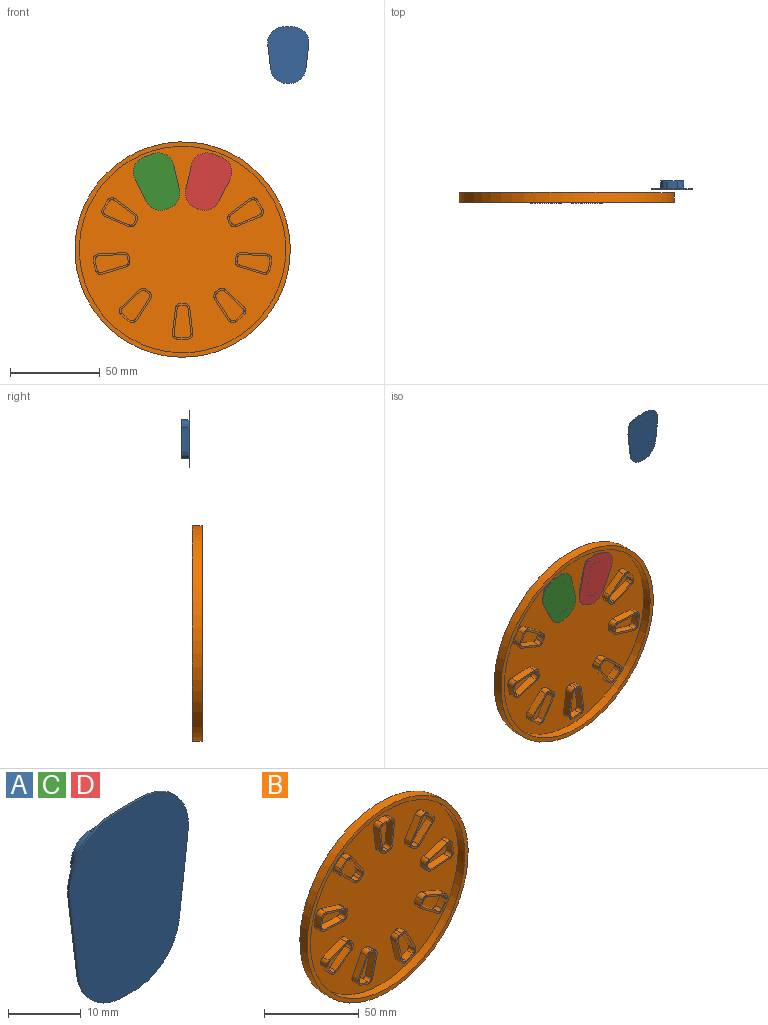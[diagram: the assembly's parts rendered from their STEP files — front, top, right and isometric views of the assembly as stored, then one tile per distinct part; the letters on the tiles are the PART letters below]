
ASSEMBLY  parts=4 mates=2
PART A: 28 faces, bbox 23.1x4.8x31.6 mm
  f0: plane 13.94x4.4mm, normal (-0.99,0,-0.12), area 61.8mm2, adj f1,f15,f16,f26
  f1: cylinder r=3.8mm len=4.4mm, axis (0,-1,0), area 24.7mm2, adj f0,f2,f16,f26
  f2: cylinder r=29.2mm len=4.4mm, axis (0,-1,0), area 8mm2, adj f1,f3,f16,f26
  f3: cylinder r=3.8mm len=4.4mm, axis (0,-1,0), area 24.7mm2, adj f2,f4,f16,f26
  f4: plane 13.94x4.4mm, normal (0.99,0,-0.12), area 61.8mm2, adj f3,f5,f16,f26
  f5: cylinder r=3.8mm len=4.4mm, axis (0,-1,0), area 27.3mm2, adj f4,f6,f16,f26
  f6: cylinder r=50.8mm len=5.92mm, axis (0,-1,0), area 26.1mm2, adj f5,f15,f16,f26
  f7: cylinder r=3.2mm len=4.4mm, axis (0,-1,0), area 23mm2, adj f8,f14,f16,f27
  f8: cylinder r=50.2mm len=5.85mm, axis (0,-1,0), area 25.8mm2, adj f7,f9,f16,f27
  f9: cylinder r=3.2mm len=4.4mm, axis (0,-1,0), area 23mm2, adj f8,f10,f16,f27
  f10: plane 13.94x4.4mm, normal (-0.99,0,0.12), area 61.8mm2, adj f9,f11,f16,f27
  f11: cylinder r=3.2mm len=4.4mm, axis (0,-1,0), area 20.8mm2, adj f10,f12,f16,f27
  f12: cylinder r=29.8mm len=4.4mm, axis (0,-1,0), area 8.2mm2, adj f11,f13,f16,f27
  f13: cylinder r=3.2mm len=4.4mm, axis (0,-1,0), area 20.8mm2, adj f12,f14,f16,f27
  f14: plane 13.94x4.4mm, normal (0.99,0,0.12), area 61.8mm2, adj f7,f13,f16,f27
  f15: cylinder r=3.8mm len=4.4mm, axis (0,-1,0), area 27.3mm2, adj f0,f6,f16,f26
  f16: plane 21.62x13.08mm, normal (0,1,0), area 34.6mm2, adj f0,f1,f2,f3,f4,f5,f6,f7
  f17: plane 31.62x23.08mm, normal (0,-1,0), area 609.5mm2, adj f18,f19,f20,f21,f22,f23,f24,f25
  f18: cylinder r=8.8mm len=9.86mm, axis (0,1,0), area 5.8mm2, adj f17,f19,f25,f26
  f19: plane 13.94x1.71mm, normal (0.99,0,-0.12), area 5.6mm2, adj f17,f18,f20,f26
  f20: cylinder r=8.8mm len=9.01mm, axis (0,1,0), area 5.2mm2, adj f17,f19,f21,f26
  f21: cylinder r=24.2mm len=1.51mm, axis (0,1,0), area 0.6mm2, adj f17,f20,f22,f26
  f22: cylinder r=8.8mm len=9.01mm, axis (0,1,0), area 5.2mm2, adj f17,f21,f23,f26
  f23: plane 13.94x1.71mm, normal (-0.99,0,-0.12), area 5.6mm2, adj f17,f22,f24,f26
  f24: cylinder r=8.8mm len=9.86mm, axis (0,1,0), area 5.8mm2, adj f17,f23,f25,f26
  f25: cylinder r=55.8mm len=6.5mm, axis (0,1,0), area 2.6mm2, adj f17,f18,f24,f26
  f26: plane 31.62x23.08mm, normal (0,1,0), area 376mm2, adj f0,f1,f2,f3,f4,f5,f6,f15
  f27: plane 20.42x11.88mm, normal (0,1,0), area 198.9mm2, adj f7,f8,f9,f10,f11,f12,f13,f14
PART B: 167 faces, bbox 120x5.4x120 mm
  f0: plane 115x115mm, normal (0,-1,0), area 8696mm2, adj f3,f5,f6,f7,f8,f9,f10,f11
  f1: cylinder r=60mm len=120mm, axis (0,1,0), area 2035.8mm2, adj f2,f4
  f2: plane 120x120mm, normal (0,1,0), area 11309.7mm2, adj f1
  f3: cylinder r=57.5mm len=115mm, axis (0,1,0), area 1806.4mm2, adj f0,f4
  f4: plane 120x120mm, normal (0,-1,0), area 922.8mm2, adj f1,f3
  f5: plane 13.94x4.5mm, normal (0.99,0,-0.12), area 63.2mm2, adj f0,f6,f20,f21
  f6: cylinder r=3mm len=4.5mm, axis (0,1,0), area 22.1mm2, adj f0,f5,f7,f21
  f7: cylinder r=50mm len=5.83mm, axis (0,1,0), area 26.2mm2, adj f0,f6,f8,f21
  f8: cylinder r=3mm len=4.5mm, axis (0,1,0), area 22.1mm2, adj f0,f7,f9,f21
  f9: plane 13.94x4.5mm, normal (-0.99,0,-0.12), area 63.2mm2, adj f0,f8,f10,f21
  f10: cylinder r=3mm len=4.5mm, axis (0,1,0), area 20mm2, adj f0,f9,f11,f21
  f11: cylinder r=30mm len=4.5mm, axis (0,1,0), area 8.4mm2, adj f0,f10,f20,f21
  f12: cylinder r=2mm len=4.5mm, axis (0,1,0), area 14.7mm2, adj f13,f19,f21,f22
  f13: cylinder r=49mm len=5.71mm, axis (0,1,0), area 25.7mm2, adj f12,f14,f21,f22
  f14: cylinder r=2mm len=4.5mm, axis (0,1,0), area 14.7mm2, adj f13,f15,f21,f22
  f15: plane 13.94x4.5mm, normal (-0.99,0,0.12), area 63.2mm2, adj f14,f16,f21,f22
  f16: cylinder r=2mm len=4.5mm, axis (0,1,0), area 13.3mm2, adj f15,f17,f21,f22
  f17: cylinder r=31mm len=4.5mm, axis (0,1,0), area 8.7mm2, adj f16,f18,f21,f22
  f18: cylinder r=2mm len=4.5mm, axis (0,1,0), area 13.3mm2, adj f17,f19,f21,f22
  f19: plane 13.94x4.5mm, normal (0.99,0,0.12), area 63.2mm2, adj f12,f18,f21,f22
  f20: cylinder r=3mm len=4.5mm, axis (0,1,0), area 20mm2, adj f0,f5,f11,f21
  f21: plane 20.02x11.48mm, normal (0,-1,0), area 51.3mm2, adj f5,f6,f7,f8,f9,f10,f11,f12
  f22: plane 18.02x9.48mm, normal (0,-1,0), area 136.6mm2, adj f12,f13,f14,f15,f16,f17,f18,f19
  f23: cylinder r=3mm len=4.5mm, axis (0,1,0), area 22.1mm2, adj f0,f24,f38,f39
  f24: cylinder r=50mm len=4.5mm, axis (0,1,0), area 26.2mm2, adj f0,f23,f25,f39
  f25: cylinder r=3mm len=4.5mm, axis (0,1,0), area 22.1mm2, adj f0,f24,f26,f39
  f26: plane 10.27x9.58mm, normal (-0.68,0,-0.73), area 63.2mm2, adj f0,f25,f27,f39
  f27: cylinder r=3mm len=4.5mm, axis (0,1,0), area 20mm2, adj f0,f26,f28,f39
  f28: cylinder r=30mm len=4.5mm, axis (0,1,0), area 8.4mm2, adj f0,f27,f29,f39
  f29: cylinder r=3mm len=4.5mm, axis (0,1,0), area 20mm2, adj f0,f28,f38,f39
  f30: cylinder r=2mm len=4.5mm, axis (0,1,0), area 13.3mm2, adj f31,f37,f39,f40
  f31: cylinder r=31mm len=4.5mm, axis (0,1,0), area 8.7mm2, adj f30,f32,f39,f40
  f32: cylinder r=2mm len=4.5mm, axis (0,1,0), area 13.3mm2, adj f31,f33,f39,f40
  f33: plane 10.27x9.58mm, normal (0.68,0,0.73), area 63.2mm2, adj f32,f34,f39,f40
  f34: cylinder r=2mm len=4.5mm, axis (0,1,0), area 14.7mm2, adj f33,f35,f39,f40
  f35: cylinder r=49mm len=4.5mm, axis (0,1,0), area 25.7mm2, adj f34,f36,f39,f40
  f36: cylinder r=2mm len=4.5mm, axis (0,1,0), area 14.7mm2, adj f35,f37,f39,f40
  f37: plane 11.78x7.65mm, normal (-0.84,0,-0.54), area 63.2mm2, adj f30,f36,f39,f40
  f38: plane 11.78x7.65mm, normal (0.84,0,0.54), area 63.2mm2, adj f0,f23,f29,f39
  f39: plane 19.1x17.84mm, normal (0,-1,0), area 51.3mm2, adj f23,f24,f25,f26,f27,f28,f29,f30
  f40: plane 17.1x15.84mm, normal (0,-1,0), area 136.6mm2, adj f30,f31,f32,f33,f34,f35,f36,f37
  f41: cylinder r=3mm len=4.5mm, axis (0,1,0), area 22.1mm2, adj f0,f42,f56,f57
  f42: cylinder r=50mm len=5.74mm, axis (0,1,0), area 26.2mm2, adj f0,f41,f43,f57
  f43: cylinder r=3mm len=4.5mm, axis (0,1,0), area 22.1mm2, adj f0,f42,f44,f57
  f44: plane 14.02x4.5mm, normal (-0.05,0,-1), area 63.2mm2, adj f0,f43,f45,f57
  f45: cylinder r=3mm len=4.5mm, axis (0,1,0), area 20mm2, adj f0,f44,f46,f57
  f46: cylinder r=30mm len=4.5mm, axis (0,1,0), area 8.4mm2, adj f0,f45,f47,f57
  f47: cylinder r=3mm len=4.5mm, axis (0,1,0), area 20mm2, adj f0,f46,f56,f57
  f48: cylinder r=2mm len=4.5mm, axis (0,1,0), area 13.3mm2, adj f49,f55,f57,f58
  f49: cylinder r=31mm len=4.5mm, axis (0,1,0), area 8.7mm2, adj f48,f50,f57,f58
  f50: cylinder r=2mm len=4.5mm, axis (0,1,0), area 13.3mm2, adj f49,f51,f57,f58
  f51: plane 14.02x4.5mm, normal (0.05,0,1), area 63.2mm2, adj f50,f52,f57,f58
  f52: cylinder r=2mm len=4.5mm, axis (0,1,0), area 14.7mm2, adj f51,f53,f57,f58
  f53: cylinder r=49mm len=5.62mm, axis (0,1,0), area 25.7mm2, adj f52,f54,f57,f58
  f54: cylinder r=2mm len=4.5mm, axis (0,1,0), area 14.7mm2, adj f53,f55,f57,f58
  f55: plane 13.43x4.5mm, normal (-0.29,0,-0.96), area 63.2mm2, adj f48,f54,f57,f58
  f56: plane 13.43x4.5mm, normal (0.29,0,0.96), area 63.2mm2, adj f0,f41,f47,f57
  f57: plane 20.38x12.13mm, normal (0,-1,0), area 51.3mm2, adj f41,f42,f43,f44,f45,f46,f47,f48
  f58: plane 18.38x10.13mm, normal (0,-1,0), area 136.6mm2, adj f48,f49,f50,f51,f52,f53,f54,f55
  f59: cylinder r=3mm len=4.5mm, axis (0,1,0), area 22.1mm2, adj f0,f60,f74,f75
  f60: cylinder r=50mm len=5.05mm, axis (0,1,0), area 26.2mm2, adj f0,f59,f61,f75
  f61: cylinder r=3mm len=4.5mm, axis (0,1,0), area 22.1mm2, adj f0,f60,f62,f75
  f62: plane 11.21x8.45mm, normal (0.6,0,-0.8), area 63.2mm2, adj f0,f61,f63,f75
  f63: cylinder r=3mm len=4.5mm, axis (0,1,0), area 20mm2, adj f0,f62,f64,f75
  f64: cylinder r=30mm len=4.5mm, axis (0,1,0), area 8.4mm2, adj f0,f63,f65,f75
  f65: cylinder r=3mm len=4.5mm, axis (0,1,0), area 20mm2, adj f0,f64,f74,f75
  f66: cylinder r=2mm len=4.5mm, axis (0,1,0), area 13.3mm2, adj f67,f73,f75,f76
  f67: cylinder r=31mm len=4.5mm, axis (0,1,0), area 8.7mm2, adj f66,f68,f75,f76
  f68: cylinder r=2mm len=4.5mm, axis (0,1,0), area 13.3mm2, adj f67,f69,f75,f76
  f69: plane 11.21x8.45mm, normal (-0.6,0,0.8), area 63.2mm2, adj f68,f70,f75,f76
  f70: cylinder r=2mm len=4.5mm, axis (0,1,0), area 14.7mm2, adj f69,f71,f75,f76
  f71: cylinder r=49mm len=4.95mm, axis (0,1,0), area 25.7mm2, adj f70,f72,f75,f76
  f72: cylinder r=2mm len=4.5mm, axis (0,1,0), area 14.7mm2, adj f71,f73,f75,f76
  f73: plane 12.92x5.49mm, normal (0.39,0,-0.92), area 63.2mm2, adj f66,f72,f75,f76
  f74: plane 12.92x5.49mm, normal (-0.39,0,0.92), area 63.2mm2, adj f0,f59,f65,f75
  f75: plane 19.95x16.23mm, normal (0,-1,0), area 51.3mm2, adj f59,f60,f61,f62,f63,f64,f65,f66
  f76: plane 17.95x14.23mm, normal (0,-1,0), area 136.6mm2, adj f66,f67,f68,f69,f70,f71,f72,f73
  f77: cylinder r=3mm len=4.5mm, axis (0,1,0), area 22.1mm2, adj f0,f78,f92,f93
  f78: cylinder r=50mm len=5.48mm, axis (0,1,0), area 26.2mm2, adj f0,f77,f79,f93
  f79: cylinder r=3mm len=4.5mm, axis (0,1,0), area 22.1mm2, adj f0,f78,f80,f93
  f80: plane 13.68x4.5mm, normal (0.97,0,-0.22), area 63.2mm2, adj f0,f79,f81,f93
  f81: cylinder r=3mm len=4.5mm, axis (0,1,0), area 20mm2, adj f0,f80,f82,f93
  f82: cylinder r=30mm len=4.5mm, axis (0,1,0), area 8.4mm2, adj f0,f81,f83,f93
  f83: cylinder r=3mm len=4.5mm, axis (0,1,0), area 20mm2, adj f0,f82,f92,f93
  f84: cylinder r=2mm len=4.5mm, axis (0,1,0), area 13.3mm2, adj f85,f91,f93,f94
  f85: cylinder r=31mm len=4.5mm, axis (0,1,0), area 8.7mm2, adj f84,f86,f93,f94
  f86: cylinder r=2mm len=4.5mm, axis (0,1,0), area 13.3mm2, adj f85,f87,f93,f94
  f87: plane 13.68x4.5mm, normal (-0.97,0,0.22), area 63.2mm2, adj f86,f88,f93,f94
  f88: cylinder r=2mm len=4.5mm, axis (0,1,0), area 14.7mm2, adj f87,f89,f93,f94
  f89: cylinder r=49mm len=5.37mm, axis (0,1,0), area 25.7mm2, adj f88,f90,f93,f94
  f90: cylinder r=2mm len=4.5mm, axis (0,1,0), area 14.7mm2, adj f89,f91,f93,f94
  f91: plane 12.51x6.37mm, normal (0.89,0,-0.45), area 63.2mm2, adj f84,f90,f93,f94
  f92: plane 12.51x6.37mm, normal (-0.89,0,0.45), area 63.2mm2, adj f0,f77,f83,f93
  f93: plane 20.38x14.31mm, normal (0,-1,0), area 51.3mm2, adj f77,f78,f79,f80,f81,f82,f83,f84
  f94: plane 18.38x12.31mm, normal (0,-1,0), area 136.6mm2, adj f84,f85,f86,f87,f88,f89,f90,f91
  f95: cylinder r=3mm len=4.5mm, axis (0,1,0), area 22.1mm2, adj f0,f96,f110,f111
  f96: cylinder r=50mm len=5.48mm, axis (0,1,0), area 26.2mm2, adj f0,f95,f97,f111
  f97: cylinder r=3mm len=4.5mm, axis (0,1,0), area 22.1mm2, adj f0,f96,f98,f111
  f98: plane 12.51x6.37mm, normal (0.89,0,0.45), area 63.2mm2, adj f0,f97,f99,f111
  f99: cylinder r=3mm len=4.5mm, axis (0,1,0), area 20mm2, adj f0,f98,f100,f111
  f100: cylinder r=30mm len=4.5mm, axis (0,1,0), area 8.4mm2, adj f0,f99,f101,f111
  f101: cylinder r=3mm len=4.5mm, axis (0,1,0), area 20mm2, adj f0,f100,f110,f111
  f102: cylinder r=2mm len=4.5mm, axis (0,1,0), area 13.3mm2, adj f103,f109,f111,f112
  f103: cylinder r=31mm len=4.5mm, axis (0,1,0), area 8.7mm2, adj f102,f104,f111,f112
  f104: cylinder r=2mm len=4.5mm, axis (0,1,0), area 13.3mm2, adj f103,f105,f111,f112
  f105: plane 12.51x6.37mm, normal (-0.89,0,-0.45), area 63.2mm2, adj f104,f106,f111,f112
  f106: cylinder r=2mm len=4.5mm, axis (0,1,0), area 14.7mm2, adj f105,f107,f111,f112
  f107: cylinder r=49mm len=5.37mm, axis (0,1,0), area 25.7mm2, adj f106,f108,f111,f112
  f108: cylinder r=2mm len=4.5mm, axis (0,1,0), area 14.7mm2, adj f107,f109,f111,f112
  f109: plane 13.68x4.5mm, normal (0.97,0,0.22), area 63.2mm2, adj f102,f108,f111,f112
  f110: plane 13.68x4.5mm, normal (-0.97,0,-0.22), area 63.2mm2, adj f0,f95,f101,f111
  f111: plane 20.38x14.31mm, normal (0,-1,0), area 51.3mm2, adj f95,f96,f97,f98,f99,f100,f101,f102
  f112: plane 18.38x12.31mm, normal (0,-1,0), area 136.6mm2, adj f102,f103,f104,f105,f106,f107,f108,f109
  f113: cylinder r=3mm len=4.5mm, axis (0,1,0), area 22.1mm2, adj f0,f114,f128,f129
  f114: cylinder r=50mm len=5.05mm, axis (0,1,0), area 26.2mm2, adj f0,f113,f115,f129
  f115: cylinder r=3mm len=4.5mm, axis (0,1,0), area 22.1mm2, adj f0,f114,f116,f129
  f116: plane 12.92x5.49mm, normal (0.39,0,0.92), area 63.2mm2, adj f0,f115,f117,f129
  f117: cylinder r=3mm len=4.5mm, axis (0,1,0), area 20mm2, adj f0,f116,f118,f129
  f118: cylinder r=30mm len=4.5mm, axis (0,1,0), area 8.4mm2, adj f0,f117,f119,f129
  f119: cylinder r=3mm len=4.5mm, axis (0,1,0), area 20mm2, adj f0,f118,f128,f129
  f120: cylinder r=2mm len=4.5mm, axis (0,1,0), area 13.3mm2, adj f121,f127,f129,f130
  f121: cylinder r=31mm len=4.5mm, axis (0,1,0), area 8.7mm2, adj f120,f122,f129,f130
  f122: cylinder r=2mm len=4.5mm, axis (0,1,0), area 13.3mm2, adj f121,f123,f129,f130
  f123: plane 12.92x5.49mm, normal (-0.39,0,-0.92), area 63.2mm2, adj f122,f124,f129,f130
  f124: cylinder r=2mm len=4.5mm, axis (0,1,0), area 14.7mm2, adj f123,f125,f129,f130
  f125: cylinder r=49mm len=4.95mm, axis (0,1,0), area 25.7mm2, adj f124,f126,f129,f130
  f126: cylinder r=2mm len=4.5mm, axis (0,1,0), area 14.7mm2, adj f125,f127,f129,f130
  f127: plane 11.21x8.45mm, normal (0.6,0,0.8), area 63.2mm2, adj f120,f126,f129,f130
  f128: plane 11.21x8.45mm, normal (-0.6,0,-0.8), area 63.2mm2, adj f0,f113,f119,f129
  f129: plane 19.95x16.23mm, normal (0,-1,0), area 51.3mm2, adj f113,f114,f115,f116,f117,f118,f119,f120
  f130: plane 17.95x14.23mm, normal (0,-1,0), area 136.6mm2, adj f120,f121,f122,f123,f124,f125,f126,f127
  f131: cylinder r=3mm len=4.5mm, axis (0,1,0), area 22.1mm2, adj f0,f132,f146,f147
  f132: cylinder r=50mm len=5.74mm, axis (0,1,0), area 26.2mm2, adj f0,f131,f133,f147
  f133: cylinder r=3mm len=4.5mm, axis (0,1,0), area 22.1mm2, adj f0,f132,f134,f147
  f134: plane 13.43x4.5mm, normal (-0.29,0,0.96), area 63.2mm2, adj f0,f133,f135,f147
  f135: cylinder r=3mm len=4.5mm, axis (0,1,0), area 20mm2, adj f0,f134,f136,f147
  f136: cylinder r=30mm len=4.5mm, axis (0,1,0), area 8.4mm2, adj f0,f135,f137,f147
  f137: cylinder r=3mm len=4.5mm, axis (0,1,0), area 20mm2, adj f0,f136,f146,f147
  f138: cylinder r=2mm len=4.5mm, axis (0,1,0), area 13.3mm2, adj f139,f145,f147,f148
  f139: cylinder r=31mm len=4.5mm, axis (0,1,0), area 8.7mm2, adj f138,f140,f147,f148
  f140: cylinder r=2mm len=4.5mm, axis (0,1,0), area 13.3mm2, adj f139,f141,f147,f148
  f141: plane 13.43x4.5mm, normal (0.29,0,-0.96), area 63.2mm2, adj f140,f142,f147,f148
  f142: cylinder r=2mm len=4.5mm, axis (0,1,0), area 14.7mm2, adj f141,f143,f147,f148
  f143: cylinder r=49mm len=5.62mm, axis (0,1,0), area 25.7mm2, adj f142,f144,f147,f148
  f144: cylinder r=2mm len=4.5mm, axis (0,1,0), area 14.7mm2, adj f143,f145,f147,f148
  f145: plane 14.02x4.5mm, normal (-0.05,0,1), area 63.2mm2, adj f138,f144,f147,f148
  f146: plane 14.02x4.5mm, normal (0.05,0,-1), area 63.2mm2, adj f0,f131,f137,f147
  f147: plane 20.38x12.13mm, normal (0,-1,0), area 51.3mm2, adj f131,f132,f133,f134,f135,f136,f137,f138
  f148: plane 18.38x10.13mm, normal (0,-1,0), area 136.6mm2, adj f138,f139,f140,f141,f142,f143,f144,f145
  f149: cylinder r=3mm len=4.5mm, axis (0,1,0), area 22.1mm2, adj f0,f150,f164,f165
  f150: cylinder r=50mm len=4.5mm, axis (0,1,0), area 26.2mm2, adj f0,f149,f151,f165
  f151: cylinder r=3mm len=4.5mm, axis (0,1,0), area 22.1mm2, adj f0,f150,f152,f165
  f152: plane 11.78x7.65mm, normal (-0.84,0,0.54), area 63.2mm2, adj f0,f151,f153,f165
  f153: cylinder r=3mm len=4.5mm, axis (0,1,0), area 20mm2, adj f0,f152,f154,f165
  f154: cylinder r=30mm len=4.5mm, axis (0,1,0), area 8.4mm2, adj f0,f153,f155,f165
  f155: cylinder r=3mm len=4.5mm, axis (0,1,0), area 20mm2, adj f0,f154,f164,f165
  f156: cylinder r=2mm len=4.5mm, axis (0,1,0), area 13.3mm2, adj f157,f163,f165,f166
  f157: cylinder r=31mm len=4.5mm, axis (0,1,0), area 8.7mm2, adj f156,f158,f165,f166
  f158: cylinder r=2mm len=4.5mm, axis (0,1,0), area 13.3mm2, adj f157,f159,f165,f166
  f159: plane 11.78x7.65mm, normal (0.84,0,-0.54), area 63.2mm2, adj f158,f160,f165,f166
  f160: cylinder r=2mm len=4.5mm, axis (0,1,0), area 14.7mm2, adj f159,f161,f165,f166
  f161: cylinder r=49mm len=4.5mm, axis (0,1,0), area 25.7mm2, adj f160,f162,f165,f166
  f162: cylinder r=2mm len=4.5mm, axis (0,1,0), area 14.7mm2, adj f161,f163,f165,f166
  f163: plane 10.27x9.58mm, normal (-0.68,0,0.73), area 63.2mm2, adj f156,f162,f165,f166
  f164: plane 10.27x9.58mm, normal (0.68,0,-0.73), area 63.2mm2, adj f0,f149,f155,f165
  f165: plane 19.1x17.84mm, normal (0,-1,0), area 51.3mm2, adj f149,f150,f151,f152,f153,f154,f155,f156
  f166: plane 17.1x15.84mm, normal (0,-1,0), area 136.6mm2, adj f156,f157,f158,f159,f160,f161,f162,f163
PART C: same geometry as A
PART D: same geometry as A
PLACE A at identity
PLACE B rot(axis=(0,-1,0),20deg) t=(-58.86,-6.8,-68.32)mm
PLACE C rot(axis=(0,-1,0),20deg) t=(-58.88,-7.3,-68.26)mm
PLACE D rot(axis=(0,1,0),20deg) t=(-58.84,-7.3,-68.26)mm
MATE revolute D.f27 <-> B.f4  axis (0,1,0) through (-44.91,-12.2,-30)mm
MATE revolute C.f27 <-> B.f4  axis (0,1,0) through (-72.81,-12.2,-30)mm
